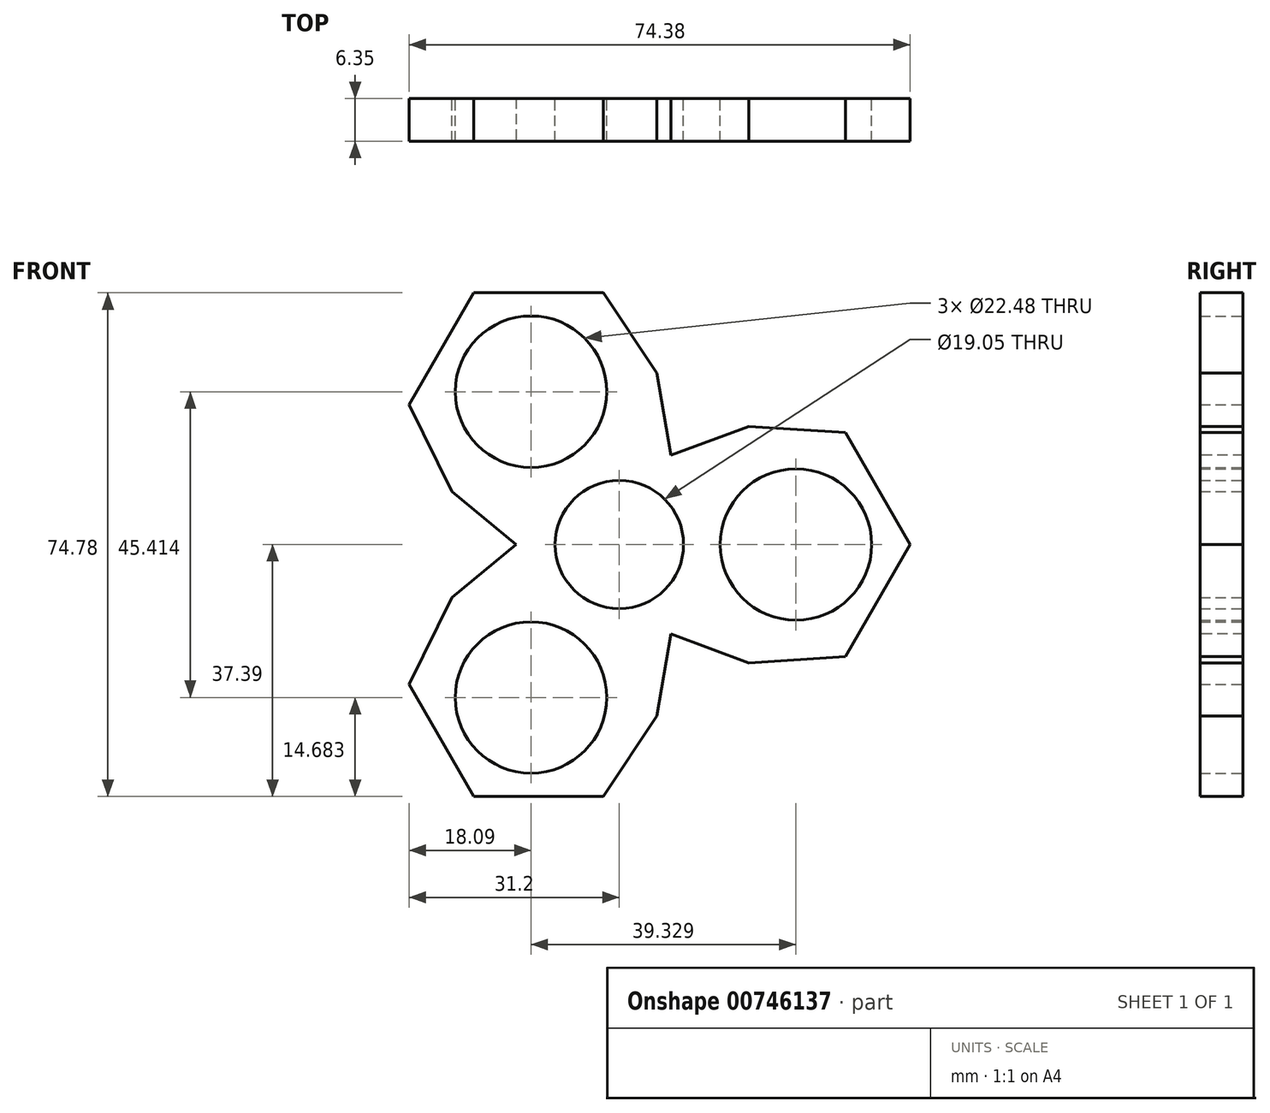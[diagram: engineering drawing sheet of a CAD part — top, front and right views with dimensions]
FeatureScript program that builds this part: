
annotation { "Feature Type Name" : "Feature", "Feature Type Description" : "" }
export const myFeature = defineFeature(function(context is Context, id is Id, definition is map)
    precondition{}
    {
        {
            var Q0;
            Q0=qCreatedBy(makeId("Front.planeOp"),FACE);
            var sketch = newSketch(context, id + "F0", { "sketchPlane" : qUnion([Q0])});
            skLineSegment(sketch, "E0.0", {"start": v(33.57, 16.65) * mm, "end": v(42.45, 1.27) * mm});
            skLineSegment(sketch, "E0.1", {"start": v(42.45, -1.27) * mm, "end": v(33.57, -16.65) * mm});
            skLineSegment(sketch, "E0.2", {"start": v(-2.36, -37.4) * mm, "end": v(-20.12, -37.4) * mm});
            skLineSegment(sketch, "E0.3", {"start": v(-22.32, -36.12) * mm, "end": v(-31.2, -20.75) * mm});
            skLineSegment(sketch, "E0.4", {"start": v(-31.2, 20.75) * mm, "end": v(-22.32, 36.12) * mm});
            skLineSegment(sketch, "E0.5", {"start": v(-20.12, 37.4) * mm, "end": v(-2.36, 37.4) * mm});
            skPoint(sketch, "E0.0.midPoint", {"position": v(32.38, 18.7) * mm});
            skPoint(sketch, "E1.visualSharp", {"position": v(-43.18, 0) * mm});
            skPoint(sketch, "E2.visualSharp", {"position": v(-21.59, 37.4) * mm});
            skArc(sketch, "E2.filletArc", {"start": v(-20.12, 37.4) * mm, "mid": v(-21.4, 37.05) * mm, "end": v(-22.32, 36.12) * mm});
            skPoint(sketch, "E3.visualSharp", {"position": v(21.6, 37.4) * mm});
            skPoint(sketch, "E4.visualSharp", {"position": v(43.18, 0) * mm});
            skArc(sketch, "E4.filletArc", {"start": v(42.45, -1.27) * mm, "mid": v(42.79, 0) * mm, "end": v(42.45, 1.27) * mm});
            skPoint(sketch, "E5.visualSharp", {"position": v(21.6, -37.4) * mm});
            skPoint(sketch, "E6.visualSharp", {"position": v(-21.59, -37.4) * mm});
            skArc(sketch, "E6.filletArc", {"start": v(-22.32, -36.12) * mm, "mid": v(-21.4, -37.05) * mm, "end": v(-20.12, -37.4) * mm});
            skCircle(sketch, "E7", {"center": v(0, 0) * mm, "radius": 9.53 * mm});
            skCircle(sketch, "E8", {"center": v(-13.1, -22.7) * mm, "radius": 11.24 * mm});
            skCircle(sketch, "E9.MirrorC", {"center": v(26.22, 0) * mm, "radius": 11.24 * mm});
            skCircle(sketch, "E10.MirrorC", {"center": v(-13.1, 22.7) * mm, "radius": 11.24 * mm});
            skLineSegment(sketch, "E11.trimOffspring", {"start": v(-21.4, -37.05) * mm, "end": v(-21.59, -37.4) * mm});
            skLineSegment(sketch, "E12", {"start": v(-2.36, -37.4) * mm, "end": v(-2.32, -37.32) * mm});
            skLineSegment(sketch, "E13", {"start": v(5.58, -25.44) * mm, "end": v(7.68, -13.3) * mm});
            skLineSegment(sketch, "E14.MirrorCS", {"start": v(19.24, -17.55) * mm, "end": v(7.68, -13.3) * mm});
            skLineSegment(sketch, "E15.MirrorCS", {"start": v(19.24, 17.55) * mm, "end": v(7.68, 13.3) * mm});
            skLineSegment(sketch, "E16.MirrorCS", {"start": v(33.57, 16.65) * mm, "end": v(19.24, 17.55) * mm});
            skLineSegment(sketch, "E17.MirrorCS", {"start": v(5.58, 25.44) * mm, "end": v(7.68, 13.3) * mm});
            skLineSegment(sketch, "E18.MirrorCS", {"start": v(-2.36, 37.4) * mm, "end": v(5.58, 25.44) * mm});
            skLineSegment(sketch, "E19.MirrorCS", {"start": v(33.57, -16.65) * mm, "end": v(42.45, -1.27) * mm});
            skPoint(sketch, "E20.MirrorP", {"position": v(21.59, -37.4) * mm});
            skPoint(sketch, "E21.MirrorCS.end.orphan", {"position": v(42.45, -73.52) * mm});
            skPoint(sketch, "E21.MirrorCS.start.orphan", {"position": v(22.32, -38.67) * mm});
            skPoint(sketch, "E22.MirrorCS.end.orphan", {"position": v(20.12, -37.4) * mm});
            skPoint(sketch, "E22.MirrorCS.start.orphan", {"position": v(0, -37.4) * mm});
            skPoint(sketch, "E23.orphan", {"position": v(22.32, -36.12) * mm});
            skLineSegment(sketch, "E24.MirrorCS", {"start": v(-24.82, -7.89) * mm, "end": v(-15.35, 0) * mm});
            skLineSegment(sketch, "E25.MirrorCS", {"start": v(-24.82, 7.89) * mm, "end": v(-15.35, 0) * mm});
            skLineSegment(sketch, "E26.MirrorCS", {"start": v(-31.2, 20.75) * mm, "end": v(-31.16, 20.67) * mm});
            skLineSegment(sketch, "E27.MirrorCS", {"start": v(-31.2, -20.75) * mm, "end": v(-31.16, -20.67) * mm});
            skPoint(sketch, "E1.filletArc.end.orphan", {"position": v(-42.45, -1.27) * mm});
            skLineSegment(sketch, "E28", {"start": v(7.68, 13.3) * mm, "end": v(19.24, 17.55) * mm});
            skLineSegment(sketch, "E29", {"start": v(-15.35, 0) * mm, "end": v(-24.82, 7.89) * mm});
            skCircle(sketch, "E30.cCircle", {"center": v(0, 0) * mm, "radius": 37.4 * mm, "construction": true});
            skLineSegment(sketch, "E30.0", {"start": v(33.57, 16.65) * mm, "end": v(43.18, 0) * mm});
            skLineSegment(sketch, "E30.1", {"start": v(43.18, 0) * mm, "end": v(32.39, -18.7) * mm});
            skLineSegment(sketch, "E30.3", {"start": v(-21.59, -37.4) * mm, "end": v(-32.38, -18.7) * mm});
            skLineSegment(sketch, "E30.4", {"start": v(-32.39, 18.7) * mm, "end": v(-21.6, 37.4) * mm});
            skLineSegment(sketch, "E30.5", {"start": v(-21.6, 37.4) * mm, "end": v(-2.36, 37.4) * mm});
            skPoint(sketch, "E31.MirrorCS.start.orphan", {"position": v(16.1, -34.22) * mm});
            skPoint(sketch, "E32.0.start.orphan", {"position": v(21.6, -31.04) * mm});
            skLineSegment(sketch, "E33.trimOffspring", {"start": v(1.86, -31.04) * mm, "end": v(5.58, -25.44) * mm});
            skLineSegment(sketch, "E34.trimOffspring", {"start": v(25.96, -17.13) * mm, "end": v(19.24, -17.55) * mm});
            skPoint(sketch, "E35.orphan", {"position": v(21.59, 37.4) * mm});
            skPoint(sketch, "E36.orphan", {"position": v(-31.05, -2.77) * mm});
            skPoint(sketch, "E37.orphan", {"position": v(-31.05, 2.77) * mm});
            skPoint(sketch, "E38.orphan", {"position": v(-23.02, 11.15) * mm});
            skPoint(sketch, "E39.orphan", {"position": v(-23.02, -11.15) * mm});
            skLineSegment(sketch, "E40.trimOffspring", {"start": v(-24.86, -7.96) * mm, "end": v(-24.82, -7.89) * mm});
            skLineSegment(sketch, "E41.trimOffspring", {"start": v(-24.86, 7.96) * mm, "end": v(-24.82, 7.89) * mm});
            skLineSegment(sketch, "E42", {"start": v(19.24, -17.55) * mm, "end": v(33.57, -16.65) * mm});
            skLineSegment(sketch, "E43", {"start": v(5.58, -25.44) * mm, "end": v(-2.32, -37.32) * mm});
            skLineSegment(sketch, "E44.trimOffspring", {"start": v(0, -37.4) * mm, "end": v(-21.59, -37.4) * mm});
            skLineSegment(sketch, "E45", {"start": v(0, 0) * mm, "end": v(-13.1, -22.7) * mm});
            skLineSegment(sketch, "E46.MirrorCS", {"start": v(-24.82, -7.89) * mm, "end": v(-31.16, -20.67) * mm});
            skLineSegment(sketch, "E47.MirrorCS", {"start": v(-27.81, 13.92) * mm, "end": v(-24.82, 7.89) * mm});
            skLineSegment(sketch, "E48.MirrorCS", {"start": v(-24.82, 7.89) * mm, "end": v(-31.2, 20.75) * mm});
            skSolve(sketch);
        }
        {
            var Q0;
            Q0=qSketchRegion(id+"F0",true);
            extrude(context, id + "F1", {"entities" : qUnion([Q0]), "depth" : 6.35 * mm, "offsetDistance" : 25.4 * mm});
        }
    });
